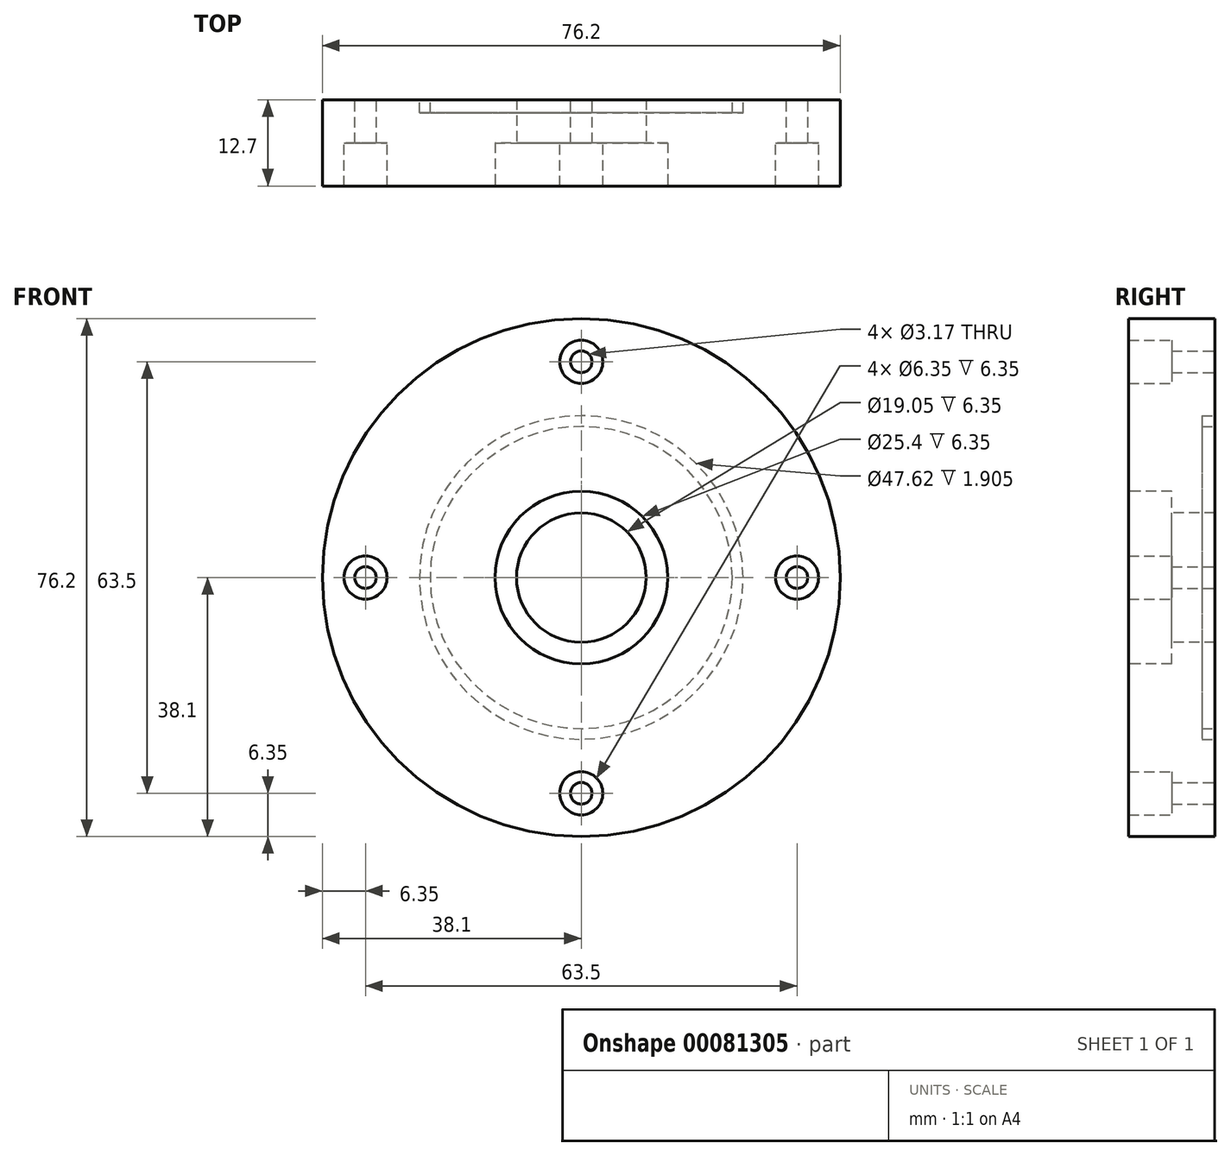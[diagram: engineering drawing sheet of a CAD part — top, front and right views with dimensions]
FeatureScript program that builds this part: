
annotation { "Feature Type Name" : "Feature", "Feature Type Description" : "" }
export const myFeature = defineFeature(function(context is Context, id is Id, definition is map)
    precondition{}
    {
        {
            var Q0;
            Q0=qCreatedBy(makeId("Front.planeOp"),FACE);
            var sketch = newSketch(context, id + "F0", { "sketchPlane" : qUnion([Q0])});
            skCircle(sketch, "E0", {"center": v(0, 0) * mm, "radius": 38.1 * mm});
            skCircle(sketch, "E1", {"center": v(20.71, 10.88) * mm, "radius": 0.88 * mm});
            skSolve(sketch);
        }
        {
            var Q0;
            Q0=makeQuery(id+"F0.imprint","IMPRINT",FACE,{"disambiguationData":[TD([[makeQuery(id+"F0.imprint","IMPRINT",EDGE,{"derivedFrom":sQuery(id+"F0.wireOp",EDGE,"E1")}),1.0]])]});
            var Q1;
            Q1=makeQuery(id+"F0.imprint","IMPRINT",FACE,{"disambiguationData":[TD([[makeQuery(id+"F0.imprint","IMPRINT",EDGE,{"derivedFrom":sQuery(id+"F0.wireOp",EDGE,"E0")}),1.0]])]});
            extrude(context, id + "F1", {"entities" : qUnion([Q0, Q1]), "depth" : 12.7 * mm});
        }
        {
            var Q0;
            Q0=makeQuery(id+"F1.opExtrude","CAP_FACE",FACE,{"disambiguationData":[OSD([sQuery(id+"F0.wireOp",EDGE,"E0"),sQuery(id+"F0.wireOp",EDGE,"E1")])],"isStart":false});
            var sketch = newSketch(context, id + "F2", { "sketchPlane" : qUnion([Q0])});
            skCircle(sketch, "E2", {"center": v(0, 0) * mm, "radius": 9.53 * mm});
            skSolve(sketch);
        }
        {
            var Q0;
            Q0 = qSketchRegion(id + "F2", true);
            extrude(context, id + "F3", {"entities" : qUnion([Q0]), "operationType" : NewBodyOperationType.REMOVE, "endBound" : BoundingType.THROUGH_ALL, "oppositeDirection" : true, "depth" : 25.4 * mm});
        }
        {
            var Q0;
            Q0=makeQuery(id+"F1.opExtrude","CAP_FACE",FACE,{"disambiguationData":[OSD([sQuery(id+"F0.wireOp",EDGE,"E0"),sQuery(id+"F0.wireOp",EDGE,"E1")])],"isStart":false});
            var sketch = newSketch(context, id + "F4", { "sketchPlane" : qUnion([Q0])});
            skCircle(sketch, "E3", {"center": v(0, 0) * mm, "radius": 12.7 * mm});
            skSolve(sketch);
        }
        {
            var Q0;
            Q0 = qSketchRegion(id + "F4", true);
            extrude(context, id + "F5", {"entities" : qUnion([Q0]), "operationType" : NewBodyOperationType.REMOVE, "oppositeDirection" : true, "depth" : 6.35 * mm});
        }
        {
            var Q0;
            Q0=makeQuery(id+"F1.opExtrude","CAP_FACE",FACE,{"disambiguationData":[OSD([sQuery(id+"F0.wireOp",EDGE,"E0")])],"isStart":false});
            var sketch = newSketch(context, id + "F6", { "sketchPlane" : qUnion([Q0])});
            skPoint(sketch, "E4", {"position": v(31.75, 0) * mm});
            skPoint(sketch, "E5", {"position": v(0, 31.75) * mm});
            skPoint(sketch, "E6", {"position": v(-31.75, 0) * mm});
            skPoint(sketch, "E7", {"position": v(0, -31.75) * mm});
            skSolve(sketch);
        }
        {
            var Q0;
            Q0=sQuery(id+"F6.wireOp",VERTEX,"E5");
            var Q1;
            Q1=sQuery(id+"F6.wireOp",VERTEX,"E4");
            var Q2;
            Q2=sQuery(id+"F6.wireOp",VERTEX,"E7");
            var Q3;
            Q3=sQuery(id+"F6.wireOp",VERTEX,"E6");
            var Q4;
            Q4=makeQuery(id+"F1.opExtrude","SWEPT_BODY",BODY,{"disambiguationData":[OSD([sQuery(id+"F0.wireOp",EDGE,"E0")])]});
            hole(context, id + "F7", {"style" : HoleStyle.C_BORE, "endStyle" : HoleEndStyle.THROUGH, "holeDiameter" : 3.17 * mm, "cBoreDiameter" : 6.35 * mm, "cBoreDepth" : 6.35 * mm, "locations" : qUnion([Q0, Q1, Q2, Q3]), "scope" : qUnion([Q4]), "isTappedThrough" : true});
        }
        {
            var Q0;
            Q0=makeQuery(id+"F1.opExtrude","CAP_FACE",FACE,{"disambiguationData":[OSD([sQuery(id+"F0.wireOp",EDGE,"E0")])],"isStart":true});
            var sketch = newSketch(context, id + "F8", { "sketchPlane" : qUnion([Q0])});
            skCircle(sketch, "E8", {"center": v(0, 0) * mm, "radius": 23.81 * mm});
            skCircle(sketch, "E9", {"center": v(0, 0) * mm, "radius": 22.23 * mm});
            skSolve(sketch);
        }
        {
            var Q0;
            Q0 = qSketchRegion(id + "F8", true);
            extrude(context, id + "F9", {"entities" : qUnion([Q0]), "operationType" : NewBodyOperationType.REMOVE, "oppositeDirection" : true, "depth" : 1.9 * mm});
        }
    });
